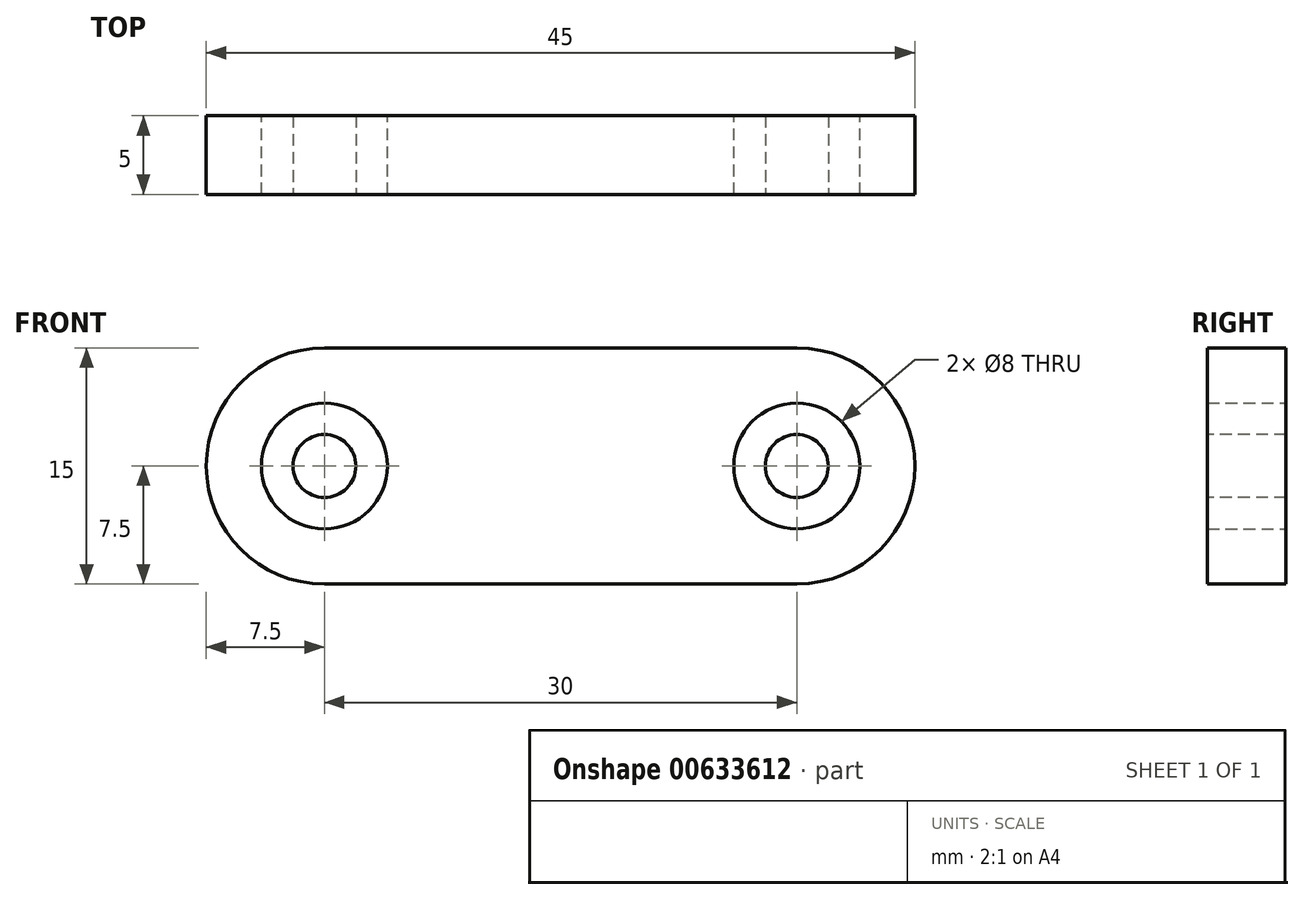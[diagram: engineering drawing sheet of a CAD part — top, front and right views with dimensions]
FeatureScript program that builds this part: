
annotation { "Feature Type Name" : "Feature", "Feature Type Description" : "" }
export const myFeature = defineFeature(function(context is Context, id is Id, definition is map)
    precondition{}
    {
        {
            var Q0;
            Q0=qCreatedBy(makeId("Front.planeOp"),FACE);
            var sketch = newSketch(context, id + "F0", { "sketchPlane" : qUnion([Q0])});
            skArc(sketch, "E0", {"start": v(0, 7.5) * mm, "mid": v(-7.5, 0) * mm, "end": v(0, -7.5) * mm});
            skArc(sketch, "E1", {"start": v(30, -7.5) * mm, "mid": v(37.5, 0) * mm, "end": v(30, 7.5) * mm});
            skLineSegment(sketch, "E2", {"start": v(0, 7.5) * mm, "end": v(30, 7.5) * mm});
            skLineSegment(sketch, "E3", {"start": v(30, -7.5) * mm, "end": v(0, -7.5) * mm});
            skCircle(sketch, "E4", {"center": v(0, 0) * mm, "radius": 4 * mm});
            skCircle(sketch, "E5", {"center": v(30, 0) * mm, "radius": 4 * mm});
            skSolve(sketch);
        }
        {
            var Q0;
            Q0=makeQuery(id+"F0.imprint","IMPRINT",FACE,{"disambiguationData":[TD([[makeQuery(id+"F0.imprint","IMPRINT",EDGE,{"derivedFrom":sQuery(id+"F0.wireOp",EDGE,"E0")}),1.0]])]});
            extrude(context, id + "F1", {"entities" : qUnion([Q0]), "depth" : 5 * mm, "offsetDistance" : 25.4 * mm});
        }
        {
            var Q0;
            Q0=makeQuery(id+"F1.opExtrude","CAP_FACE",FACE,{"disambiguationData":[OSD([sQuery(id+"F0.wireOp",EDGE,"E0"),sQuery(id+"F0.wireOp",EDGE,"E1"),sQuery(id+"F0.wireOp",EDGE,"E2"),sQuery(id+"F0.wireOp",EDGE,"E3"),sQuery(id+"F0.wireOp",EDGE,"E4"),sQuery(id+"F0.wireOp",EDGE,"E5")])],"isStart":false});
            var sketch = newSketch(context, id + "F2", { "sketchPlane" : qUnion([Q0])});
            skCircle(sketch, "E6", {"center": v(0, 0) * mm, "radius": 2 * mm});
            skCircle(sketch, "E7", {"center": v(30, 0) * mm, "radius": 2 * mm});
            skSolve(sketch);
        }
        {
            var Q0;
            Q0=makeQuery(id+"F2.imprint","IMPRINT",FACE,{"disambiguationData":[TD([[makeQuery(id+"F2.imprint","IMPRINT",EDGE,{"derivedFrom":sQuery(id+"F2.wireOp",EDGE,"E7")}),1.0]])]});
            var Q1;
            Q1=makeQuery(id+"F2.imprint","IMPRINT",FACE,{"disambiguationData":[TD([[makeQuery(id+"F2.imprint","IMPRINT",EDGE,{"derivedFrom":sQuery(id+"F2.wireOp",EDGE,"E6")}),1.0]])]});
            extrude(context, id + "F3", {"entities" : qUnion([Q0, Q1]), "oppositeDirection" : true, "depth" : 5 * mm, "offsetDistance" : 25.4 * mm});
        }
    });
